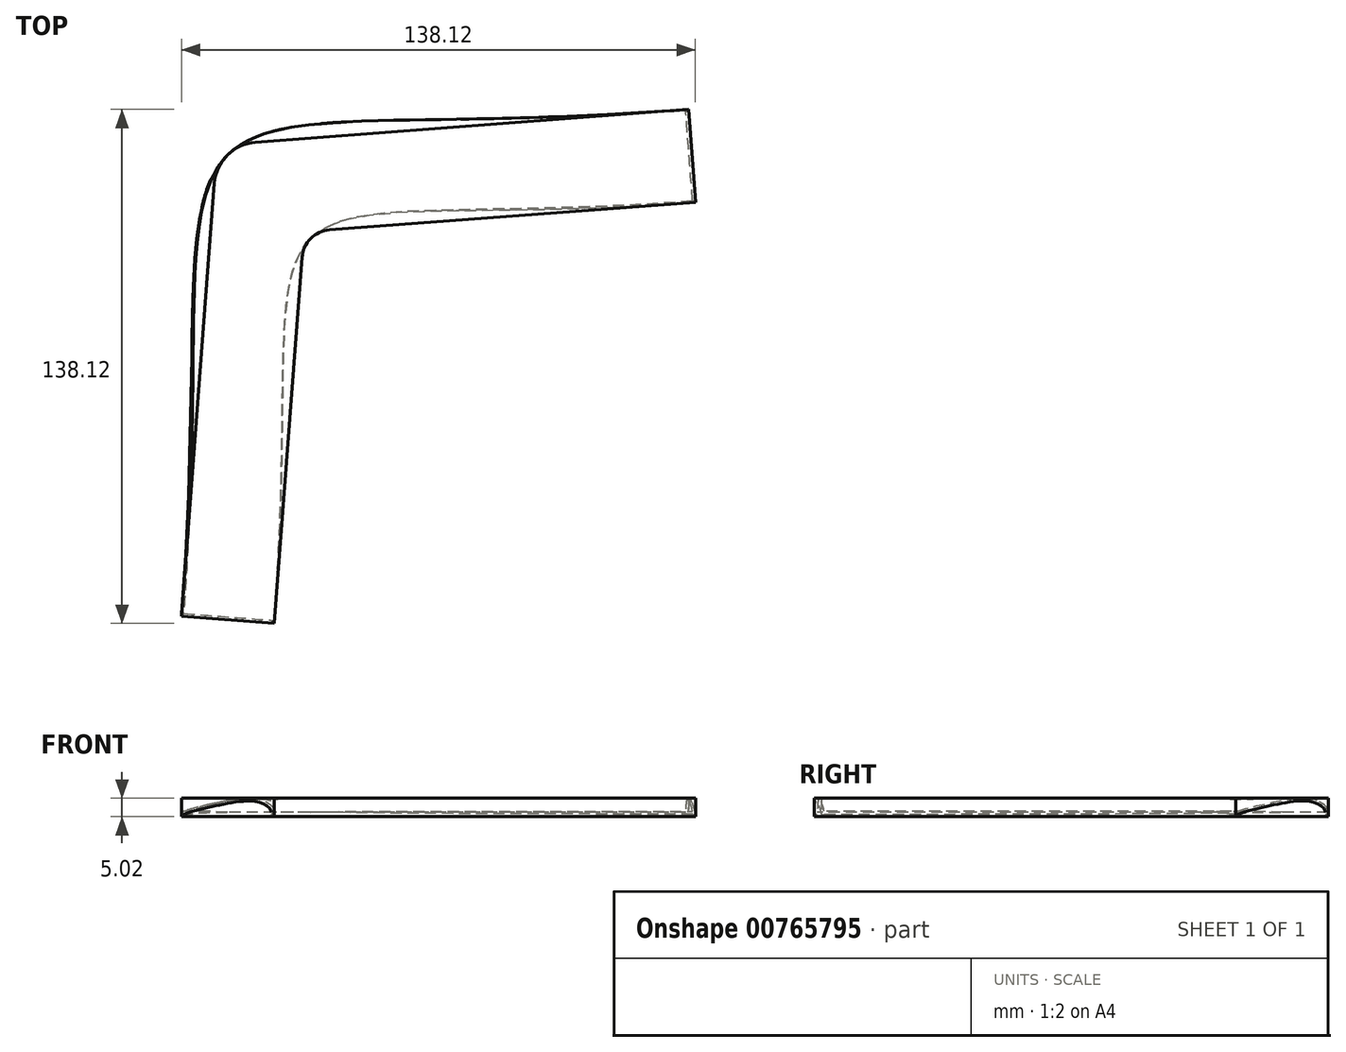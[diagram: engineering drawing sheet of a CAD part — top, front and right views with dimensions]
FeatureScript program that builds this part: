
annotation { "Feature Type Name" : "Feature", "Feature Type Description" : "" }
export const myFeature = defineFeature(function(context is Context, id is Id, definition is map)
    precondition{}
    {
        {
            var Q0;
            Q0=qCreatedBy(makeId("Top.planeOp"),FACE);
            var sketch = newSketch(context, id + "F0", { "sketchPlane" : qUnion([Q0])});
            skLineSegment(sketch, "E0.bottom", {"start": v(70, -70) * mm, "end": v(-70, -70) * mm, "construction": true});
            skLineSegment(sketch, "E0.top", {"start": v(70, 70) * mm, "end": v(-70, 70) * mm, "construction": true});
            skLineSegment(sketch, "E0.left", {"start": v(70, -70) * mm, "end": v(70, 70) * mm, "construction": true});
            skLineSegment(sketch, "E0.right", {"start": v(-70, -70) * mm, "end": v(-70, 70) * mm, "construction": true});
            skPoint(sketch, "E0.middle", {"position": v(0, 0) * mm});
            skLineSegment(sketch, "E1", {"start": v(-70, 70) * mm, "end": v(70, -70) * mm, "construction": true});
            skLineSegment(sketch, "E2", {"start": v(-70, -70) * mm, "end": v(70, 70) * mm, "construction": true});
            skLineSegment(sketch, "E3", {"start": v(-49.11, 60.17) * mm, "end": v(67.24, 69) * mm});
            skLineSegment(sketch, "E4", {"start": v(67.24, 69) * mm, "end": v(69.13, 44.06) * mm});
            skLineSegment(sketch, "E5", {"start": v(69.13, 44.06) * mm, "end": v(-29.24, 36.6) * mm});
            skLineSegment(sketch, "E6", {"start": v(-36.09, 36.09) * mm, "end": v(-59.4, 59.4) * mm});
            skLineSegment(sketch, "E7", {"start": v(69.13, 44.06) * mm, "end": v(71.13, 44.22) * mm});
            skLineSegment(sketch, "E8", {"start": v(73.9, 47.43) * mm, "end": v(72.46, 66.38) * mm});
            skLineSegment(sketch, "E9", {"start": v(69.24, 69.14) * mm, "end": v(67.24, 69) * mm});
            skPoint(sketch, "E10.visualSharp", {"position": v(74.12, 44.44) * mm});
            skArc(sketch, "E10.filletArc", {"start": v(71.13, 44.22) * mm, "mid": v(73.18, 45.25) * mm, "end": v(73.9, 47.43) * mm});
            skPoint(sketch, "E11.visualSharp", {"position": v(72.23, 69.37) * mm});
            skArc(sketch, "E11.filletArc", {"start": v(72.46, 66.38) * mm, "mid": v(71.42, 68.43) * mm, "end": v(69.24, 69.14) * mm});
            skLineSegment(sketch, "E12.MirrorCS", {"start": v(-60.17, 49.11) * mm, "end": v(-69, -67.24) * mm});
            skLineSegment(sketch, "E13.MirrorCS", {"start": v(-44.06, -69.13) * mm, "end": v(-36.6, 29.24) * mm});
            skLineSegment(sketch, "E14.MirrorCS", {"start": v(-69, -67.24) * mm, "end": v(-44.06, -69.13) * mm});
            skLineSegment(sketch, "E15.MirrorCS", {"start": v(-69.14, -69.24) * mm, "end": v(-69, -67.24) * mm});
            skArc(sketch, "E16.MirrorCS", {"start": v(-66.38, -72.46) * mm, "mid": v(-68.43, -71.42) * mm, "end": v(-69.14, -69.24) * mm});
            skLineSegment(sketch, "E17.MirrorCS", {"start": v(-47.43, -73.9) * mm, "end": v(-66.38, -72.46) * mm});
            skArc(sketch, "E18.MirrorCS", {"start": v(-44.22, -71.13) * mm, "mid": v(-45.25, -73.18) * mm, "end": v(-47.43, -73.9) * mm});
            skLineSegment(sketch, "E19.MirrorCS", {"start": v(-44.06, -69.13) * mm, "end": v(-44.22, -71.13) * mm});
            skPoint(sketch, "E20.visualSharp", {"position": v(-59.4, 59.4) * mm});
            skArc(sketch, "E20.filletArc", {"start": v(-49.11, 60.17) * mm, "mid": v(-56.7, 56.7) * mm, "end": v(-60.17, 49.11) * mm});
            skPoint(sketch, "E21.visualSharp", {"position": v(-36.09, 36.09) * mm});
            skArc(sketch, "E21.filletArc", {"start": v(-29.24, 36.6) * mm, "mid": v(-34.29, 34.29) * mm, "end": v(-36.6, 29.24) * mm});
            skLineSegment(sketch, "E22", {"start": v(-59.4, 59.4) * mm, "end": v(-26.9, 26.9) * mm});
            skSolve(sketch);
        }
        {
            var Q0;
            {var subQ2=sQuery(id+"F0.wireOp",EDGE,"E3");Q0=makeQuery(id+"F0.imprint","IMPRINT",FACE,{"disambiguationData":[TD([[makeQuery(id+"F0.imprint","IMPRINT",EDGE,{"derivedFrom":subQ2}),-1.0]])]});}
            extrude(context, id + "F1", {"entities" : qUnion([Q0]), "depth" : 5 * mm, "offsetDistance" : 25 * mm});
        }
        {
            var Q0;
            Q0=makeQuery(id+"F1.opExtrude","SWEPT_FACE",FACE,{"disambiguationData":[OSD([sQuery(id+"F0.wireOp",EDGE,"E4")])]});
            var sketch = newSketch(context, id + "F2", { "sketchPlane" : qUnion([Q0])});
            skLineSegment(sketch, "E23", {"start": v(38.71, 2.5) * mm, "end": v(63.71, 2.5) * mm, "construction": true});
            skLineSegment(sketch, "E24", {"start": v(51.21, 5) * mm, "end": v(51.21, 0) * mm, "construction": true});
            skLineSegment(sketch, "E25", {"start": v(38.71, 1.25) * mm, "end": v(63.71, 1.25) * mm, "construction": true});
            skLineSegment(sketch, "E26", {"start": v(38.71, 3.75) * mm, "end": v(63.71, 3.75) * mm, "construction": true});
            skLineSegment(sketch, "E27", {"start": v(60.21, 5) * mm, "end": v(60.21, 0) * mm, "construction": true});
            skLineSegment(sketch, "E28", {"start": v(42.21, 5) * mm, "end": v(42.21, 0) * mm, "construction": true});
            skLineSegment(sketch, "E29", {"start": v(38.71, 1.25) * mm, "end": v(38.71, 0) * mm});
            skLineSegment(sketch, "E30", {"start": v(38.71, 0) * mm, "end": v(63.71, 0) * mm});
            skLineSegment(sketch, "E31", {"start": v(63.71, 0) * mm, "end": v(63.71, 1.25) * mm});
            skFitSpline(sketch, "E32", {"points": [v(38.71, 1.25) * mm, v(42.21, 2.39) * mm, v(51.21, 4.37) * mm, v(60.21, 4.51) * mm, v(63.71, 1.25) * mm], "startDerivative": vector(22.56, 8.8) * mm, "endDerivative": vector(0, -19.7) * mm});
            skPoint(sketch, "E33", {"position": v(42.21, 2.5) * mm});
            skSolve(sketch);
        }
        {
            var Q0;
            Q0=makeQuery(id+"F1.opExtrude","SWEPT_FACE",FACE,{"disambiguationData":[OSD([sQuery(id+"F0.wireOp",EDGE,"E22")])]});
            var sketch = newSketch(context, id + "F3", { "sketchPlane" : qUnion([Q0])});
            skLineSegment(sketch, "E34", {"start": v(-80.17, 2.5) * mm, "end": v(-48.49, 2.5) * mm, "construction": true});
            skLineSegment(sketch, "E35", {"start": v(-64.33, 5) * mm, "end": v(-64.33, 0) * mm, "construction": true});
            skLineSegment(sketch, "E36", {"start": v(-80.17, 1.25) * mm, "end": v(-48.49, 1.25) * mm, "construction": true});
            skLineSegment(sketch, "E37", {"start": v(-80.17, 3.75) * mm, "end": v(-48.49, 3.75) * mm, "construction": true});
            skLineSegment(sketch, "E38", {"start": v(-56.33, 5) * mm, "end": v(-56.33, 0) * mm, "construction": true});
            skLineSegment(sketch, "E39", {"start": v(-72.33, 5) * mm, "end": v(-72.33, 0) * mm, "construction": true});
            skLineSegment(sketch, "E40", {"start": v(-80.17, 1.25) * mm, "end": v(-80.17, 0) * mm});
            skLineSegment(sketch, "E41", {"start": v(-80.17, 0) * mm, "end": v(-48.49, 0) * mm});
            skLineSegment(sketch, "E42", {"start": v(-48.49, 0) * mm, "end": v(-48.49, 1.25) * mm});
            skFitSpline(sketch, "E43", {"points": [v(-80.17, 1.25) * mm, v(-72.33, 4.4) * mm, v(-64.33, 4.78) * mm, v(-56.33, 4.4) * mm, v(-48.49, 1.25) * mm], "startDerivative": vector(0, 18.74) * mm, "endDerivative": vector(0, -19.8) * mm});
            skSolve(sketch);
        }
        {
            var Q0;
            {var subQ1=sQuery(id+"F0.wireOp",EDGE,"E12.MirrorCS");Q0=makeQuery(id+"F0.imprint","IMPRINT",FACE,{"disambiguationData":[TD([[makeQuery(id+"F0.imprint","IMPRINT",EDGE,{"derivedFrom":subQ1}),1.0]])]});}
            extrude(context, id + "F4", {"entities" : qUnion([Q0]), "operationType" : NewBodyOperationType.ADD, "depth" : 5 * mm, "offsetDistance" : 25 * mm});
        }
        {
            var Q0;
            Q0=makeQuery(id+"F4.opExtrude","SWEPT_FACE",FACE,{"disambiguationData":[OSD([sQuery(id+"F0.wireOp",EDGE,"E14.MirrorCS")])]});
            var sketch = newSketch(context, id + "F5", { "sketchPlane" : qUnion([Q0])});
            skLineSegment(sketch, "E44", {"start": v(-63.71, 2.5) * mm, "end": v(-38.71, 2.5) * mm, "construction": true});
            skLineSegment(sketch, "E45", {"start": v(-51.21, 5) * mm, "end": v(-51.21, 0) * mm, "construction": true});
            skLineSegment(sketch, "E46", {"start": v(-63.71, 1.25) * mm, "end": v(-38.71, 1.25) * mm, "construction": true});
            skLineSegment(sketch, "E47", {"start": v(-63.71, 3.75) * mm, "end": v(-38.71, 3.75) * mm, "construction": true});
            skLineSegment(sketch, "E48", {"start": v(-42.21, 5) * mm, "end": v(-42.21, 0) * mm, "construction": true});
            skLineSegment(sketch, "E49", {"start": v(-60.21, 5) * mm, "end": v(-60.21, 0) * mm, "construction": true});
            skLineSegment(sketch, "E50", {"start": v(-63.71, 1.25) * mm, "end": v(-63.71, 0) * mm});
            skLineSegment(sketch, "E51", {"start": v(-63.71, 0) * mm, "end": v(-38.71, 0) * mm});
            skLineSegment(sketch, "E52", {"start": v(-38.71, 0) * mm, "end": v(-38.71, 1.25) * mm});
            skFitSpline(sketch, "E53", {"points": [v(-63.71, 1.25) * mm, v(-60.21, 2.39) * mm, v(-51.21, 4.37) * mm, v(-42.21, 4.51) * mm, v(-38.71, 1.25) * mm], "startDerivative": vector(22.56, 8.8) * mm, "endDerivative": vector(0, -19.7) * mm});
            skPoint(sketch, "E54", {"position": v(-60.21, 2.5) * mm});
            skSolve(sketch);
        }
        {
            var Q1;
            Q1 = qSketchRegion(id + "F2", true);
            var Q2;
            Q2 = qSketchRegion(id + "F3", true);
            var Q3;
            Q3 = qSketchRegion(id + "F5", true);
            loft(context, id + "F6", {"startCondition" : LoftEndDerivativeType.NORMAL_TO_PROFILE, "startMagnitude" : 1.5, "endCondition" : LoftEndDerivativeType.NORMAL_TO_PROFILE, "endMagnitude" : 1.5, "sheetProfilesArray" : [{ "sheetProfileEntities" : qUnion([Q1]) }, { "sheetProfileEntities" : qUnion([Q2]) }, { "sheetProfileEntities" : qUnion([Q3]) }]});
        }
        {
            var Q0;
            Q0=makeQuery(id+"F6.opLoft","SWEPT_EDGE",EDGE,{"disambiguationData":[OSD([sQuery(id+"F0.wireOp",EDGE,"E12.MirrorCS"),sQuery(id+"F0.wireOp",EDGE,"E14.MirrorCS"),sQuery(id+"F0.wireOp",EDGE,"E15.MirrorCS"),sQuery(id+"F0.wireOp",EDGE,"E20.filletArc"),sQuery(id+"F0.wireOp",EDGE,"E22"),sQuery(id+"F3.wireOp",EDGE,"E40"),sQuery(id+"F3.wireOp",EDGE,"E43"),sQuery(id+"F5.wireOp",EDGE,"E50"),sQuery(id+"F5.wireOp",EDGE,"E53")])]});
            var Q1;
            Q1=makeQuery(id+"F6.opLoft","SWEPT_EDGE",EDGE,{"disambiguationData":[OSD([sQuery(id+"F0.wireOp",EDGE,"E4"),sQuery(id+"F0.wireOp",EDGE,"E5"),sQuery(id+"F0.wireOp",EDGE,"E7"),sQuery(id+"F0.wireOp",EDGE,"E21.filletArc"),sQuery(id+"F0.wireOp",EDGE,"E22"),sQuery(id+"F2.wireOp",EDGE,"E29"),sQuery(id+"F2.wireOp",EDGE,"E32"),sQuery(id+"F3.wireOp",EDGE,"E42"),sQuery(id+"F3.wireOp",EDGE,"E43")])]});
            fillet(context, id + "F7", {"entities" : qUnion([Q0, Q1]), "radius" : .75 * mm, "tangentPropagation" : true, "allowEdgeOverflow" : false});
        }
        {
            var Q0;
            Q0=makeQuery(id+"F6.opLoft","SWEPT_EDGE",EDGE,{"disambiguationData":[OSD([sQuery(id+"F2.wireOp",EDGE,"E29"),sQuery(id+"F2.wireOp",EDGE,"E30"),sQuery(id+"F3.wireOp",EDGE,"E41"),sQuery(id+"F3.wireOp",EDGE,"E42")])]});
            var Q1;
            Q1=makeQuery(id+"F6.opLoft","SWEPT_EDGE",EDGE,{"disambiguationData":[OSD([sQuery(id+"F2.wireOp",EDGE,"E30"),sQuery(id+"F2.wireOp",EDGE,"E31"),sQuery(id+"F3.wireOp",EDGE,"E40"),sQuery(id+"F3.wireOp",EDGE,"E41")])]});
            fillet(context, id + "F8", {"entities" : qUnion([Q0, Q1]), "radius" : .5 * mm, "tangentPropagation" : true, "allowEdgeOverflow" : false});
        }
        {
            var Q0;
            Q0=makeQuery(id+"F6.opLoft","MID_CAP_EDGE",EDGE,{"disambiguationData":[OSD([sQuery(id+"F0.wireOp",EDGE,"E12.MirrorCS"),sQuery(id+"F0.wireOp",EDGE,"E13.MirrorCS"),sQuery(id+"F0.wireOp",EDGE,"E14.MirrorCS"),sQuery(id+"F0.wireOp",EDGE,"E15.MirrorCS"),sQuery(id+"F0.wireOp",EDGE,"E19.MirrorCS"),sQuery(id+"F5.wireOp",EDGE,"E50"),sQuery(id+"F5.wireOp",EDGE,"E52"),sQuery(id+"F5.wireOp",EDGE,"E53")])],"capPos":2.0});
            var Q1;
            Q1=makeQuery(id+"F6.opLoft","CAP_FACE",FACE,{"disambiguationData":[OSD([makeQuery(id+"F2.imprint","IMPRINT",FACE,{"disambiguationData":[TD([[makeQuery(id+"F2.imprint","IMPRINT",EDGE,{"derivedFrom":sQuery(id+"F2.wireOp",EDGE,"E29")}),1.0]])]})])],"isStart":true});
            fillet(context, id + "F9", {"entities" : qUnion([Q0, Q1]), "radius" : .75 * mm, "tangentPropagation" : true, "allowEdgeOverflow" : false});
        }
        {
            var Q0;
            Q0=makeQuery(id+"F6.opLoft","SWEPT_BODY",BODY,{"disambiguationData":[OSD([makeQuery(id+"F2.imprint","IMPRINT",FACE,{"disambiguationData":[TD([[makeQuery(id+"F2.imprint","IMPRINT",EDGE,{"derivedFrom":sQuery(id+"F2.wireOp",EDGE,"E29")}),1.0]])]}),sQuery(id+"F3.wireOp",EDGE,"E43"),makeQuery(id+"F5.imprint","IMPRINT",FACE,{"disambiguationData":[TD([[makeQuery(id+"F5.imprint","IMPRINT",EDGE,{"derivedFrom":sQuery(id+"F5.wireOp",EDGE,"E50")}),1.0]])]})])]});
            transform(context, id + "F10", {"entities" : qUnion([Q0]), "transformType" : TransformType.TRANSLATION_3D, "dx" : 0 * mm, "dy" : 0 * mm, "dz" : 0 * mm, "makeCopy" : true});
        }
    });
